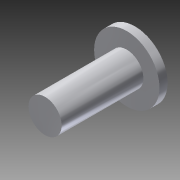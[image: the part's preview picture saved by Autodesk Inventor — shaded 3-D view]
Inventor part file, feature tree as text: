
AUTODESK INVENTOR PART (.ipt)
format: ipt  version: 2015 (Build 190159000, 159)  size: 84,992 bytes
history: native  units: mm
features: extrude x2, sketch x1
ambient origin geometry x8: Origin, YZ Plane, XZ Plane, XY Plane, X Axis, Y Axis, Z Axis, Center Point
bodies: Solid1 (feature_tree)
feature tree (3):
  sketch  "Sketch1"  dims[d0=4.064mm d1=8.0mm d2=10.0mm d3=0.0mm d4=1.0mm d5=0.0mm]
  extrude  "Extrusion1"  Depth=1.0mm
  extrude  "Extrusion2"  Depth=10.0mm TaperAngle=0.0deg
